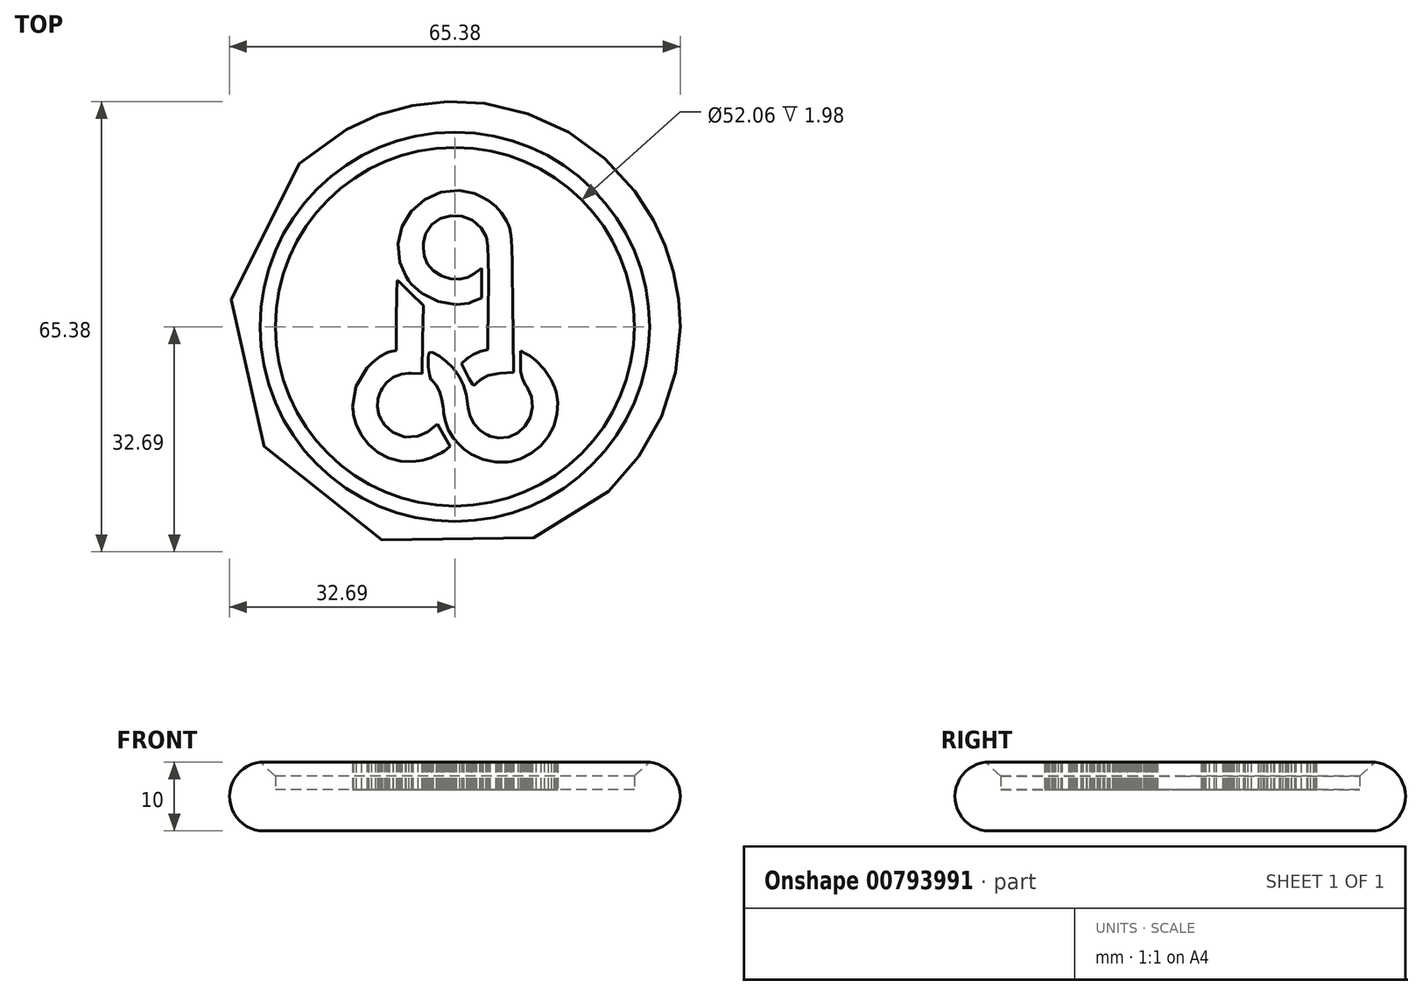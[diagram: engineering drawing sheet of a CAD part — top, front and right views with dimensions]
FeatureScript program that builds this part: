
annotation { "Feature Type Name" : "Feature", "Feature Type Description" : "" }
export const myFeature = defineFeature(function(context is Context, id is Id, definition is map)
    precondition{}
    {
        {
            var Q0;
            Q0=qCreatedBy(makeId("Top.planeOp"),FACE);
            var sketch = newSketch(context, id + "F0", { "sketchPlane" : qUnion([Q0])});
            skLineSegment(sketch, "E0", {"start": v(3.53, 19.01) * mm, "end": v(3.87, 18.86) * mm});
            skLineSegment(sketch, "E1", {"start": v(3.87, 18.86) * mm, "end": v(4.85, 18.32) * mm});
            skLineSegment(sketch, "E2", {"start": v(4.85, 18.32) * mm, "end": v(5.9, 17.52) * mm});
            skLineSegment(sketch, "E3", {"start": v(5.9, 17.52) * mm, "end": v(6.77, 16.55) * mm});
            skLineSegment(sketch, "E4", {"start": v(6.77, 16.55) * mm, "end": v(7.35, 15.66) * mm});
            skLineSegment(sketch, "E5", {"start": v(7.35, 15.66) * mm, "end": v(7.51, 15.35) * mm});
            skLineSegment(sketch, "E6", {"start": v(7.51, 15.35) * mm, "end": v(7.58, 15.23) * mm});
            skLineSegment(sketch, "E7", {"start": v(7.58, 15.23) * mm, "end": v(7.76, 14.86) * mm});
            skLineSegment(sketch, "E8", {"start": v(7.76, 14.86) * mm, "end": v(7.95, 14.33) * mm});
            skLineSegment(sketch, "E9", {"start": v(7.95, 14.33) * mm, "end": v(8.1, 13.63) * mm});
            skLineSegment(sketch, "E10", {"start": v(8.1, 13.63) * mm, "end": v(8.2, 12.66) * mm});
            skLineSegment(sketch, "E11", {"start": v(8.2, 12.66) * mm, "end": v(8.27, 11.29) * mm});
            skLineSegment(sketch, "E12", {"start": v(8.27, 11.29) * mm, "end": v(8.32, 9.41) * mm});
            skLineSegment(sketch, "E13", {"start": v(8.32, 9.41) * mm, "end": v(8.36, 6.91) * mm});
            skLineSegment(sketch, "E14", {"start": v(8.36, 6.91) * mm, "end": v(8.39, 4.48) * mm});
            skLineSegment(sketch, "E15", {"start": v(8.39, 4.48) * mm, "end": v(8.4, 3.67) * mm});
            skLineSegment(sketch, "E16", {"start": v(8.4, 3.67) * mm, "end": v(8.5, -6.6) * mm});
            skLineSegment(sketch, "E17", {"start": v(8.5, -6.6) * mm, "end": v(6.53, -6.77) * mm});
            skLineSegment(sketch, "E18", {"start": v(6.53, -6.77) * mm, "end": v(6.2, -6.8) * mm});
            skLineSegment(sketch, "E19", {"start": v(6.2, -6.8) * mm, "end": v(4.86, -7.07) * mm});
            skLineSegment(sketch, "E20", {"start": v(4.86, -7.07) * mm, "end": v(3.91, -7.56) * mm});
            skLineSegment(sketch, "E21", {"start": v(3.91, -7.56) * mm, "end": v(3.77, -7.7) * mm});
            skLineSegment(sketch, "E22", {"start": v(3.77, -7.7) * mm, "end": v(3.66, -7.8) * mm});
            skLineSegment(sketch, "E23", {"start": v(3.66, -7.8) * mm, "end": v(3.13, -8.24) * mm});
            skLineSegment(sketch, "E24", {"start": v(3.13, -8.24) * mm, "end": v(2.85, -8.47) * mm});
            skLineSegment(sketch, "E25", {"start": v(2.85, -8.47) * mm, "end": v(2.75, -8.47) * mm});
            skLineSegment(sketch, "E26", {"start": v(2.75, -8.47) * mm, "end": v(2.71, -8.47) * mm});
            skLineSegment(sketch, "E27", {"start": v(2.71, -8.47) * mm, "end": v(2.6, -8.34) * mm});
            skLineSegment(sketch, "E28", {"start": v(2.6, -8.34) * mm, "end": v(2.35, -8) * mm});
            skLineSegment(sketch, "E29", {"start": v(2.35, -8) * mm, "end": v(2.05, -7.5) * mm});
            skLineSegment(sketch, "E30", {"start": v(2.05, -7.5) * mm, "end": v(1.8, -7.03) * mm});
            skLineSegment(sketch, "E31", {"start": v(1.8, -7.03) * mm, "end": v(1.73, -6.88) * mm});
            skLineSegment(sketch, "E32", {"start": v(1.73, -6.88) * mm, "end": v(0.95, -5.33) * mm});
            skLineSegment(sketch, "E33", {"start": v(0.95, -5.33) * mm, "end": v(1.8, -4.62) * mm});
            skLineSegment(sketch, "E34", {"start": v(1.8, -4.62) * mm, "end": v(1.91, -4.52) * mm});
            skLineSegment(sketch, "E35", {"start": v(1.91, -4.52) * mm, "end": v(2.71, -4.02) * mm});
            skLineSegment(sketch, "E36", {"start": v(2.71, -4.02) * mm, "end": v(3.56, -3.64) * mm});
            skLineSegment(sketch, "E37", {"start": v(3.56, -3.64) * mm, "end": v(3.7, -3.6) * mm});
            skLineSegment(sketch, "E38", {"start": v(3.7, -3.6) * mm, "end": v(4.76, -3.32) * mm});
            skLineSegment(sketch, "E39", {"start": v(4.76, -3.32) * mm, "end": v(4.87, 4.1) * mm});
            skLineSegment(sketch, "E40", {"start": v(4.87, 4.1) * mm, "end": v(4.88, 4.86) * mm});
            skLineSegment(sketch, "E41", {"start": v(4.88, 4.86) * mm, "end": v(4.89, 7.17) * mm});
            skLineSegment(sketch, "E42", {"start": v(4.89, 7.17) * mm, "end": v(4.85, 9.76) * mm});
            skLineSegment(sketch, "E43", {"start": v(4.85, 9.76) * mm, "end": v(4.76, 11.67) * mm});
            skLineSegment(sketch, "E44", {"start": v(4.76, 11.67) * mm, "end": v(4.67, 12.52) * mm});
            skLineSegment(sketch, "E45", {"start": v(4.67, 12.52) * mm, "end": v(4.62, 12.7) * mm});
            skLineSegment(sketch, "E46", {"start": v(4.62, 12.7) * mm, "end": v(4.5, 13.13) * mm});
            skLineSegment(sketch, "E47", {"start": v(4.5, 13.13) * mm, "end": v(3.8, 14.34) * mm});
            skLineSegment(sketch, "E48", {"start": v(3.8, 14.34) * mm, "end": v(2.56, 15.45) * mm});
            skLineSegment(sketch, "E49", {"start": v(2.56, 15.45) * mm, "end": v(1.06, 16.03) * mm});
            skLineSegment(sketch, "E50", {"start": v(1.06, 16.03) * mm, "end": v(-0.54, 16.11) * mm});
            skLineSegment(sketch, "E51", {"start": v(-0.54, 16.11) * mm, "end": v(-2.06, 15.7) * mm});
            skLineSegment(sketch, "E52", {"start": v(-2.06, 15.7) * mm, "end": v(-3.36, 14.83) * mm});
            skLineSegment(sketch, "E53", {"start": v(-3.36, 14.83) * mm, "end": v(-4.25, 13.5) * mm});
            skLineSegment(sketch, "E54", {"start": v(-4.25, 13.5) * mm, "end": v(-4.59, 12.19) * mm});
            skLineSegment(sketch, "E55", {"start": v(-4.59, 12.19) * mm, "end": v(-4.59, 11.75) * mm});
            skLineSegment(sketch, "E56", {"start": v(-4.59, 11.75) * mm, "end": v(-4.59, 11.38) * mm});
            skLineSegment(sketch, "E57", {"start": v(-4.59, 11.38) * mm, "end": v(-4.44, 10.3) * mm});
            skLineSegment(sketch, "E58", {"start": v(-4.44, 10.3) * mm, "end": v(-3.97, 9.12) * mm});
            skLineSegment(sketch, "E59", {"start": v(-3.97, 9.12) * mm, "end": v(-3.16, 8.17) * mm});
            skLineSegment(sketch, "E60", {"start": v(-3.16, 8.17) * mm, "end": v(-2.29, 7.57) * mm});
            skLineSegment(sketch, "E61", {"start": v(-2.29, 7.57) * mm, "end": v(-1.98, 7.4) * mm});
            skLineSegment(sketch, "E62", {"start": v(-1.98, 7.4) * mm, "end": v(-1.66, 7.26) * mm});
            skLineSegment(sketch, "E63", {"start": v(-1.66, 7.26) * mm, "end": v(-0.64, 6.96) * mm});
            skLineSegment(sketch, "E64", {"start": v(-0.64, 6.96) * mm, "end": v(0.64, 6.88) * mm});
            skLineSegment(sketch, "E65", {"start": v(0.64, 6.88) * mm, "end": v(1.86, 7.17) * mm});
            skLineSegment(sketch, "E66", {"start": v(1.86, 7.17) * mm, "end": v(2.74, 7.63) * mm});
            skLineSegment(sketch, "E67", {"start": v(2.74, 7.63) * mm, "end": v(3, 7.83) * mm});
            skLineSegment(sketch, "E68", {"start": v(3, 7.83) * mm, "end": v(3.88, 8.5) * mm});
            skLineSegment(sketch, "E69", {"start": v(3.88, 8.5) * mm, "end": v(3.88, 4.2) * mm});
            skLineSegment(sketch, "E70", {"start": v(3.88, 4.2) * mm, "end": v(2.58, 3.63) * mm});
            skLineSegment(sketch, "E71", {"start": v(2.58, 3.63) * mm, "end": v(2.03, 3.4) * mm});
            skLineSegment(sketch, "E72", {"start": v(2.03, 3.4) * mm, "end": v(0.2, 3.21) * mm});
            skLineSegment(sketch, "E73", {"start": v(0.2, 3.21) * mm, "end": v(-2.37, 3.67) * mm});
            skLineSegment(sketch, "E74", {"start": v(-2.37, 3.67) * mm, "end": v(-4.78, 4.88) * mm});
            skLineSegment(sketch, "E75", {"start": v(-4.78, 4.88) * mm, "end": v(-6.32, 6.2) * mm});
            skLineSegment(sketch, "E76", {"start": v(-6.32, 6.2) * mm, "end": v(-6.7, 6.74) * mm});
            skLineSegment(sketch, "E77", {"start": v(-6.7, 6.74) * mm, "end": v(-7.12, 7.32) * mm});
            skLineSegment(sketch, "E78", {"start": v(-7.12, 7.32) * mm, "end": v(-7.99, 9.37) * mm});
            skLineSegment(sketch, "E79", {"start": v(-7.99, 9.37) * mm, "end": v(-8.25, 12.02) * mm});
            skLineSegment(sketch, "E80", {"start": v(-8.25, 12.02) * mm, "end": v(-7.65, 14.54) * mm});
            skLineSegment(sketch, "E81", {"start": v(-7.65, 14.54) * mm, "end": v(-6.31, 16.74) * mm});
            skLineSegment(sketch, "E82", {"start": v(-6.31, 16.74) * mm, "end": v(-4.38, 18.46) * mm});
            skLineSegment(sketch, "E83", {"start": v(-4.38, 18.46) * mm, "end": v(-2, 19.53) * mm});
            skLineSegment(sketch, "E84", {"start": v(-2, 19.53) * mm, "end": v(0.68, 19.77) * mm});
            skLineSegment(sketch, "E85", {"start": v(0.68, 19.77) * mm, "end": v(2.87, 19.31) * mm});
            skLineSegment(sketch, "E86", {"start": v(2.87, 19.31) * mm, "end": v(3.53, 19.01) * mm});
            skLineSegment(sketch, "E87", {"start": v(-6.39, 4.87) * mm, "end": v(-4.55, 3.07) * mm});
            skLineSegment(sketch, "E88", {"start": v(-4.55, 3.07) * mm, "end": v(-4.66, -1.9) * mm});
            skLineSegment(sketch, "E89", {"start": v(-4.66, -1.9) * mm, "end": v(-4.76, -6.84) * mm});
            skLineSegment(sketch, "E90", {"start": v(-4.76, -6.84) * mm, "end": v(-6.35, -6.77) * mm});
            skLineSegment(sketch, "E91", {"start": v(-6.35, -6.77) * mm, "end": v(-6.7, -6.75) * mm});
            skLineSegment(sketch, "E92", {"start": v(-6.7, -6.75) * mm, "end": v(-7.75, -6.88) * mm});
            skLineSegment(sketch, "E93", {"start": v(-7.75, -6.88) * mm, "end": v(-8.96, -7.34) * mm});
            skLineSegment(sketch, "E94", {"start": v(-8.96, -7.34) * mm, "end": v(-9.95, -8.14) * mm});
            skLineSegment(sketch, "E95", {"start": v(-9.95, -8.14) * mm, "end": v(-10.55, -8.97) * mm});
            skLineSegment(sketch, "E96", {"start": v(-10.55, -8.97) * mm, "end": v(-10.69, -9.28) * mm});
            skLineSegment(sketch, "E97", {"start": v(-10.69, -9.28) * mm, "end": v(-10.83, -9.57) * mm});
            skLineSegment(sketch, "E98", {"start": v(-10.83, -9.57) * mm, "end": v(-11.13, -10.5) * mm});
            skLineSegment(sketch, "E99", {"start": v(-11.13, -10.5) * mm, "end": v(-11.24, -11.64) * mm});
            skLineSegment(sketch, "E100", {"start": v(-11.24, -11.64) * mm, "end": v(-11.03, -12.73) * mm});
            skLineSegment(sketch, "E101", {"start": v(-11.03, -12.73) * mm, "end": v(-10.64, -13.55) * mm});
            skLineSegment(sketch, "E102", {"start": v(-10.64, -13.55) * mm, "end": v(-10.48, -13.8) * mm});
            skLineSegment(sketch, "E103", {"start": v(-10.48, -13.8) * mm, "end": v(-10.2, -14.22) * mm});
            skLineSegment(sketch, "E104", {"start": v(-10.2, -14.22) * mm, "end": v(-9.01, -15.3) * mm});
            skLineSegment(sketch, "E105", {"start": v(-9.01, -15.3) * mm, "end": v(-7.23, -16.02) * mm});
            skLineSegment(sketch, "E106", {"start": v(-7.23, -16.02) * mm, "end": v(-5.35, -15.92) * mm});
            skLineSegment(sketch, "E107", {"start": v(-5.35, -15.92) * mm, "end": v(-3.94, -15.28) * mm});
            skLineSegment(sketch, "E108", {"start": v(-3.94, -15.28) * mm, "end": v(-3.56, -14.96) * mm});
            skLineSegment(sketch, "E109", {"start": v(-3.56, -14.96) * mm, "end": v(-2.54, -14.11) * mm});
            skLineSegment(sketch, "E110", {"start": v(-2.54, -14.11) * mm, "end": v(-1.62, -15.73) * mm});
            skLineSegment(sketch, "E111", {"start": v(-1.62, -15.73) * mm, "end": v(-0.7, -17.36) * mm});
            skLineSegment(sketch, "E112", {"start": v(-0.7, -17.36) * mm, "end": v(-1.52, -18.03) * mm});
            skLineSegment(sketch, "E113", {"start": v(-1.52, -18.03) * mm, "end": v(-1.62, -18.11) * mm});
            skLineSegment(sketch, "E114", {"start": v(-1.62, -18.11) * mm, "end": v(-1.97, -18.32) * mm});
            skLineSegment(sketch, "E115", {"start": v(-1.97, -18.32) * mm, "end": v(-2.64, -18.66) * mm});
            skLineSegment(sketch, "E116", {"start": v(-2.64, -18.66) * mm, "end": v(-3.42, -18.98) * mm});
            skLineSegment(sketch, "E117", {"start": v(-3.42, -18.98) * mm, "end": v(-4.03, -19.2) * mm});
            skLineSegment(sketch, "E118", {"start": v(-4.03, -19.2) * mm, "end": v(-4.23, -19.26) * mm});
            skLineSegment(sketch, "E119", {"start": v(-4.23, -19.26) * mm, "end": v(-4.68, -19.4) * mm});
            skLineSegment(sketch, "E120", {"start": v(-4.68, -19.4) * mm, "end": v(-6.07, -19.6) * mm});
            skLineSegment(sketch, "E121", {"start": v(-6.07, -19.6) * mm, "end": v(-7.88, -19.51) * mm});
            skLineSegment(sketch, "E122", {"start": v(-7.88, -19.51) * mm, "end": v(-9.58, -19.04) * mm});
            skLineSegment(sketch, "E123", {"start": v(-9.58, -19.04) * mm, "end": v(-11.14, -18.23) * mm});
            skLineSegment(sketch, "E124", {"start": v(-11.14, -18.23) * mm, "end": v(-12.5, -17.12) * mm});
            skLineSegment(sketch, "E125", {"start": v(-12.5, -17.12) * mm, "end": v(-13.58, -15.73) * mm});
            skLineSegment(sketch, "E126", {"start": v(-13.58, -15.73) * mm, "end": v(-14.36, -14.12) * mm});
            skLineSegment(sketch, "E127", {"start": v(-14.36, -14.12) * mm, "end": v(-14.7, -12.77) * mm});
            skLineSegment(sketch, "E128", {"start": v(-14.7, -12.77) * mm, "end": v(-14.75, -12.31) * mm});
            skLineSegment(sketch, "E129", {"start": v(-14.75, -12.31) * mm, "end": v(-14.8, -11.63) * mm});
            skLineSegment(sketch, "E130", {"start": v(-14.8, -11.63) * mm, "end": v(-14.33, -8.63) * mm});
            skLineSegment(sketch, "E131", {"start": v(-14.33, -8.63) * mm, "end": v(-12.76, -6.02) * mm});
            skLineSegment(sketch, "E132", {"start": v(-12.76, -6.02) * mm, "end": v(-12.28, -5.54) * mm});
            skLineSegment(sketch, "E133", {"start": v(-12.28, -5.54) * mm, "end": v(-12.1, -5.36) * mm});
            skLineSegment(sketch, "E134", {"start": v(-12.1, -5.36) * mm, "end": v(-11.54, -4.86) * mm});
            skLineSegment(sketch, "E135", {"start": v(-11.54, -4.86) * mm, "end": v(-10.78, -4.29) * mm});
            skLineSegment(sketch, "E136", {"start": v(-10.78, -4.29) * mm, "end": v(-10.1, -3.87) * mm});
            skLineSegment(sketch, "E137", {"start": v(-10.1, -3.87) * mm, "end": v(-9.67, -3.7) * mm});
            skLineSegment(sketch, "E138", {"start": v(-9.67, -3.7) * mm, "end": v(-9.53, -3.67) * mm});
            skLineSegment(sketch, "E139", {"start": v(-9.53, -3.67) * mm, "end": v(-8.47, -3.42) * mm});
            skLineSegment(sketch, "E140", {"start": v(-8.47, -3.42) * mm, "end": v(-8.47, 1.62) * mm});
            skLineSegment(sketch, "E141", {"start": v(-8.47, 1.62) * mm, "end": v(-8.47, 2.12) * mm});
            skLineSegment(sketch, "E142", {"start": v(-8.47, 2.12) * mm, "end": v(-8.46, 3.6) * mm});
            skLineSegment(sketch, "E143", {"start": v(-8.46, 3.6) * mm, "end": v(-8.42, 5.2) * mm});
            skLineSegment(sketch, "E144", {"start": v(-8.42, 5.2) * mm, "end": v(-8.38, 6.3) * mm});
            skLineSegment(sketch, "E145", {"start": v(-8.38, 6.3) * mm, "end": v(-8.34, 6.7) * mm});
            skLineSegment(sketch, "E146", {"start": v(-8.34, 6.7) * mm, "end": v(-8.33, 6.7) * mm});
            skLineSegment(sketch, "E147", {"start": v(-8.33, 6.7) * mm, "end": v(-8.28, 6.7) * mm});
            skLineSegment(sketch, "E148", {"start": v(-8.28, 6.7) * mm, "end": v(-8.14, 6.56) * mm});
            skLineSegment(sketch, "E149", {"start": v(-8.14, 6.56) * mm, "end": v(-7.71, 6.17) * mm});
            skLineSegment(sketch, "E150", {"start": v(-7.71, 6.17) * mm, "end": v(-7.11, 5.59) * mm});
            skLineSegment(sketch, "E151", {"start": v(-7.11, 5.59) * mm, "end": v(-6.57, 5.05) * mm});
            skLineSegment(sketch, "E152", {"start": v(-6.57, 5.05) * mm, "end": v(-6.39, 4.87) * mm});
            skLineSegment(sketch, "E153", {"start": v(-0.14, -6.17) * mm, "end": v(0.08, -6.42) * mm});
            skLineSegment(sketch, "E154", {"start": v(0.08, -6.42) * mm, "end": v(0.67, -7.23) * mm});
            skLineSegment(sketch, "E155", {"start": v(0.67, -7.23) * mm, "end": v(1.24, -8.4) * mm});
            skLineSegment(sketch, "E156", {"start": v(1.24, -8.4) * mm, "end": v(1.64, -9.84) * mm});
            skLineSegment(sketch, "E157", {"start": v(1.64, -9.84) * mm, "end": v(1.88, -11.24) * mm});
            skLineSegment(sketch, "E158", {"start": v(1.88, -11.24) * mm, "end": v(1.94, -11.71) * mm});
            skLineSegment(sketch, "E159", {"start": v(1.94, -11.71) * mm, "end": v(1.98, -12.05) * mm});
            skLineSegment(sketch, "E160", {"start": v(1.98, -12.05) * mm, "end": v(2.24, -13.03) * mm});
            skLineSegment(sketch, "E161", {"start": v(2.24, -13.03) * mm, "end": v(2.8, -14.12) * mm});
            skLineSegment(sketch, "E162", {"start": v(2.8, -14.12) * mm, "end": v(3.63, -15) * mm});
            skLineSegment(sketch, "E163", {"start": v(3.63, -15) * mm, "end": v(4.46, -15.55) * mm});
            skLineSegment(sketch, "E164", {"start": v(4.46, -15.55) * mm, "end": v(4.76, -15.7) * mm});
            skLineSegment(sketch, "E165", {"start": v(4.76, -15.7) * mm, "end": v(5.13, -15.87) * mm});
            skLineSegment(sketch, "E166", {"start": v(5.13, -15.87) * mm, "end": v(6.34, -16.14) * mm});
            skLineSegment(sketch, "E167", {"start": v(6.34, -16.14) * mm, "end": v(7.82, -16) * mm});
            skLineSegment(sketch, "E168", {"start": v(7.82, -16) * mm, "end": v(9.13, -15.4) * mm});
            skLineSegment(sketch, "E169", {"start": v(9.13, -15.4) * mm, "end": v(10.2, -14.42) * mm});
            skLineSegment(sketch, "E170", {"start": v(10.2, -14.42) * mm, "end": v(10.93, -13.17) * mm});
            skLineSegment(sketch, "E171", {"start": v(10.93, -13.17) * mm, "end": v(11.26, -11.72) * mm});
            skLineSegment(sketch, "E172", {"start": v(11.26, -11.72) * mm, "end": v(11.1, -10.2) * mm});
            skLineSegment(sketch, "E173", {"start": v(11.1, -10.2) * mm, "end": v(10.64, -9.02) * mm});
            skLineSegment(sketch, "E174", {"start": v(10.64, -9.02) * mm, "end": v(10.4, -8.68) * mm});
            skLineSegment(sketch, "E175", {"start": v(10.4, -8.68) * mm, "end": v(10.29, -8.5) * mm});
            skLineSegment(sketch, "E176", {"start": v(10.29, -8.5) * mm, "end": v(9.99, -7.96) * mm});
            skLineSegment(sketch, "E177", {"start": v(9.99, -7.96) * mm, "end": v(9.71, -7.24) * mm});
            skLineSegment(sketch, "E178", {"start": v(9.71, -7.24) * mm, "end": v(9.57, -6.43) * mm});
            skLineSegment(sketch, "E179", {"start": v(9.57, -6.43) * mm, "end": v(9.53, -5.68) * mm});
            skLineSegment(sketch, "E180", {"start": v(9.53, -5.68) * mm, "end": v(9.53, -5.43) * mm});
            skLineSegment(sketch, "E181", {"start": v(9.53, -5.43) * mm, "end": v(9.53, -3.5) * mm});
            skLineSegment(sketch, "E182", {"start": v(9.53, -3.5) * mm, "end": v(10.51, -4.02) * mm});
            skLineSegment(sketch, "E183", {"start": v(10.51, -4.02) * mm, "end": v(10.85, -4.2) * mm});
            skLineSegment(sketch, "E184", {"start": v(10.85, -4.2) * mm, "end": v(11.77, -4.91) * mm});
            skLineSegment(sketch, "E185", {"start": v(11.77, -4.91) * mm, "end": v(12.97, -6.2) * mm});
            skLineSegment(sketch, "E186", {"start": v(12.97, -6.2) * mm, "end": v(13.97, -7.7) * mm});
            skLineSegment(sketch, "E187", {"start": v(13.97, -7.7) * mm, "end": v(14.52, -8.84) * mm});
            skLineSegment(sketch, "E188", {"start": v(14.52, -8.84) * mm, "end": v(14.64, -9.24) * mm});
            skLineSegment(sketch, "E189", {"start": v(14.64, -9.24) * mm, "end": v(14.76, -9.67) * mm});
            skLineSegment(sketch, "E190", {"start": v(14.76, -9.67) * mm, "end": v(14.94, -11) * mm});
            skLineSegment(sketch, "E191", {"start": v(14.94, -11) * mm, "end": v(14.84, -12.75) * mm});
            skLineSegment(sketch, "E192", {"start": v(14.84, -12.75) * mm, "end": v(14.37, -14.4) * mm});
            skLineSegment(sketch, "E193", {"start": v(14.37, -14.4) * mm, "end": v(13.56, -15.94) * mm});
            skLineSegment(sketch, "E194", {"start": v(13.56, -15.94) * mm, "end": v(12.45, -17.28) * mm});
            skLineSegment(sketch, "E195", {"start": v(12.45, -17.28) * mm, "end": v(11.08, -18.37) * mm});
            skLineSegment(sketch, "E196", {"start": v(11.08, -18.37) * mm, "end": v(9.48, -19.17) * mm});
            skLineSegment(sketch, "E197", {"start": v(9.48, -19.17) * mm, "end": v(8.15, -19.55) * mm});
            skLineSegment(sketch, "E198", {"start": v(8.15, -19.55) * mm, "end": v(7.7, -19.62) * mm});
            skLineSegment(sketch, "E199", {"start": v(7.7, -19.62) * mm, "end": v(7.25, -19.68) * mm});
            skLineSegment(sketch, "E200", {"start": v(7.25, -19.68) * mm, "end": v(5.9, -19.63) * mm});
            skLineSegment(sketch, "E201", {"start": v(5.9, -19.63) * mm, "end": v(4.08, -19.23) * mm});
            skLineSegment(sketch, "E202", {"start": v(4.08, -19.23) * mm, "end": v(2.38, -18.48) * mm});
            skLineSegment(sketch, "E203", {"start": v(2.38, -18.48) * mm, "end": v(1.27, -17.73) * mm});
            skLineSegment(sketch, "E204", {"start": v(1.27, -17.73) * mm, "end": v(0.95, -17.43) * mm});
            skLineSegment(sketch, "E205", {"start": v(0.95, -17.43) * mm, "end": v(0.65, -17.14) * mm});
            skLineSegment(sketch, "E206", {"start": v(0.65, -17.14) * mm, "end": v(-0.17, -16.2) * mm});
            skLineSegment(sketch, "E207", {"start": v(-0.17, -16.2) * mm, "end": v(-0.94, -15) * mm});
            skLineSegment(sketch, "E208", {"start": v(-0.94, -15) * mm, "end": v(-1.4, -13.66) * mm});
            skLineSegment(sketch, "E209", {"start": v(-1.4, -13.66) * mm, "end": v(-1.62, -12.44) * mm});
            skLineSegment(sketch, "E210", {"start": v(-1.62, -12.44) * mm, "end": v(-1.66, -12.03) * mm});
            skLineSegment(sketch, "E211", {"start": v(-1.66, -12.03) * mm, "end": v(-1.7, -11.67) * mm});
            skLineSegment(sketch, "E212", {"start": v(-1.7, -11.67) * mm, "end": v(-1.88, -10.6) * mm});
            skLineSegment(sketch, "E213", {"start": v(-1.88, -10.6) * mm, "end": v(-2.24, -9.4) * mm});
            skLineSegment(sketch, "E214", {"start": v(-2.24, -9.4) * mm, "end": v(-2.71, -8.48) * mm});
            skLineSegment(sketch, "E215", {"start": v(-2.71, -8.48) * mm, "end": v(-3.14, -7.94) * mm});
            skLineSegment(sketch, "E216", {"start": v(-3.14, -7.94) * mm, "end": v(-3.32, -7.8) * mm});
            skLineSegment(sketch, "E217", {"start": v(-3.32, -7.8) * mm, "end": v(-3.46, -7.68) * mm});
            skLineSegment(sketch, "E218", {"start": v(-3.46, -7.68) * mm, "end": v(-3.67, -7.04) * mm});
            skLineSegment(sketch, "E219", {"start": v(-3.67, -7.04) * mm, "end": v(-3.88, -5.79) * mm});
            skLineSegment(sketch, "E220", {"start": v(-3.88, -5.79) * mm, "end": v(-3.89, -4.53) * mm});
            skLineSegment(sketch, "E221", {"start": v(-3.89, -4.53) * mm, "end": v(-3.78, -3.89) * mm});
            skLineSegment(sketch, "E222", {"start": v(-3.78, -3.89) * mm, "end": v(-3.67, -3.77) * mm});
            skLineSegment(sketch, "E223", {"start": v(-3.67, -3.77) * mm, "end": v(-3.6, -3.7) * mm});
            skLineSegment(sketch, "E224", {"start": v(-3.6, -3.7) * mm, "end": v(-3.13, -3.77) * mm});
            skLineSegment(sketch, "E225", {"start": v(-3.13, -3.77) * mm, "end": v(-2.24, -4.26) * mm});
            skLineSegment(sketch, "E226", {"start": v(-2.24, -4.26) * mm, "end": v(-1.17, -5.1) * mm});
            skLineSegment(sketch, "E227", {"start": v(-1.17, -5.1) * mm, "end": v(-0.38, -5.89) * mm});
            skLineSegment(sketch, "E228", {"start": v(-0.38, -5.89) * mm, "end": v(-0.14, -6.17) * mm});
            skCircle(sketch, "E229", {"center": v(0, 0) * mm, "radius": 26.03 * mm});
            skCircle(sketch, "E230", {"center": v(0, 0) * mm, "radius": 32.69 * mm});
            skSolve(sketch);
        }
        {
            var Q0;
            Q0=makeQuery(id+"F0.imprint","IMPRINT",FACE,{"disambiguationData":[TD([[makeQuery(id+"F0.imprint","IMPRINT",EDGE,{"derivedFrom":sQuery(id+"F0.wireOp",EDGE,"E0")}),1.0]])]});
            extrude(context, id + "F1", {"entities" : qUnion([Q0]), "depth" : 6 * mm, "offsetDistance" : 25.4 * mm});
        }
        {
            var Q0;
            Q0=makeQuery(id+"F0.imprint","IMPRINT",FACE,{"disambiguationData":[TD([[makeQuery(id+"F0.imprint","IMPRINT",EDGE,{"derivedFrom":sQuery(id+"F0.wireOp",EDGE,"E229")}),-1.0]])]});
            var Q1;
            Q1=makeQuery(id+"F0.imprint","IMPRINT",FACE,{"disambiguationData":[TD([[makeQuery(id+"F0.imprint","IMPRINT",EDGE,{"derivedFrom":sQuery(id+"F0.wireOp",EDGE,"E0")}),-1.0]])]});
            var Q2;
            Q2=makeQuery(id+"F0.imprint","IMPRINT",FACE,{"disambiguationData":[TD([[makeQuery(id+"F0.imprint","IMPRINT",EDGE,{"derivedFrom":sQuery(id+"F0.wireOp",EDGE,"E153")}),-1.0]])]});
            var Q3;
            Q3=makeQuery(id+"F0.imprint","IMPRINT",FACE,{"disambiguationData":[TD([[makeQuery(id+"F0.imprint","IMPRINT",EDGE,{"derivedFrom":sQuery(id+"F0.wireOp",EDGE,"E87")}),-1.0]])]});
            extrude(context, id + "F2", {"entities" : qUnion([Q0, Q1, Q2, Q3]), "operationType" : NewBodyOperationType.ADD, "depth" : 10 * mm, "offsetDistance" : 25 * mm});
        }
        {
            var Q0;
            Q0=makeQuery(id+"F2.opExtrude","CAP_EDGE",EDGE,{"disambiguationData":[OSD([sQuery(id+"F0.wireOp",EDGE,"E230")])],"isStart":true});
            var Q1;
            Q1=makeQuery(id+"F2.opExtrude","CAP_EDGE",EDGE,{"disambiguationData":[OSD([sQuery(id+"F0.wireOp",EDGE,"E230")])],"isStart":false});
            fillet(context, id + "F3", {"entities" : qUnion([Q0, Q1]), "radius" : 5 * mm, "tangentPropagation" : true, "allowEdgeOverflow" : false});
        }
        {
            var Q0;
            Q0=makeQuery(id+"F2.opExtrude","CAP_EDGE",EDGE,{"disambiguationData":[OSD([sQuery(id+"F0.wireOp",EDGE,"E229")])],"isStart":false});
            chamfer(context, id + "F4", {"entities" : qUnion([Q0]), "width" : 2 * mm, "tangentPropagation" : true});
        }
    });
